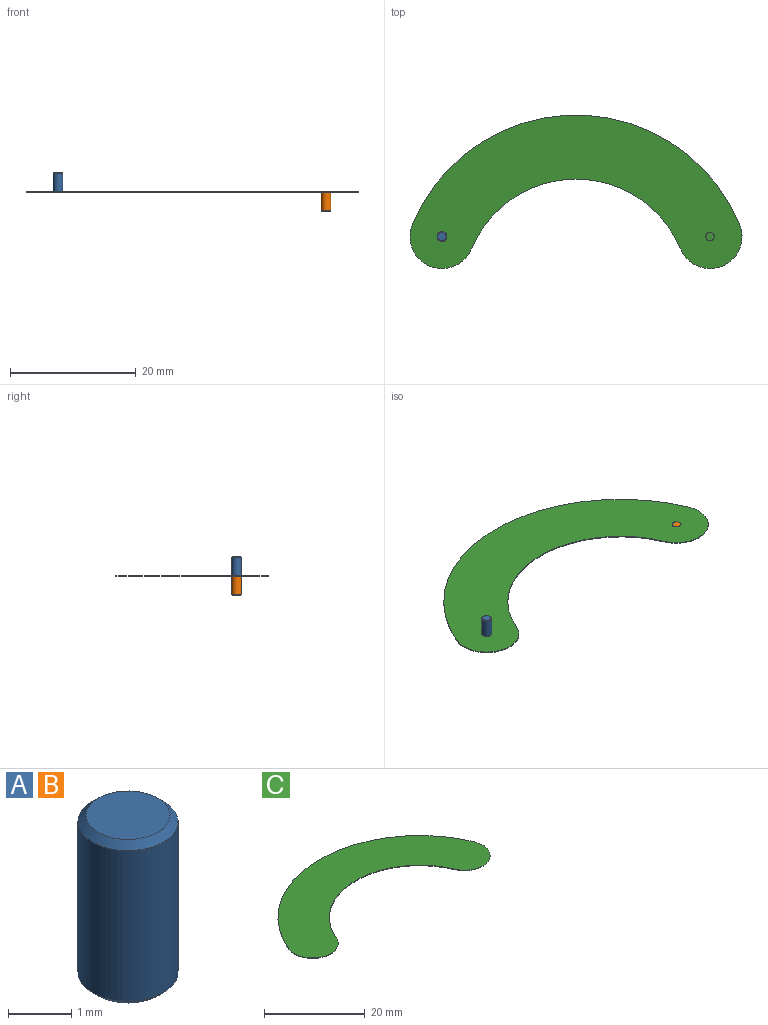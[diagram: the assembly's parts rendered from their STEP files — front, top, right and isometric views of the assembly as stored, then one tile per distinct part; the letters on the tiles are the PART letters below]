
ASSEMBLY  parts=3 mates=2
PART A: 5 faces, bbox 1.6x1.6x3.2 mm
  f0: cylinder r=0.79mm len=2.92mm, axis (0,0,-1), area 14.6mm2, adj f3,f4
  f1: plane 1.33x1.33mm, normal (0,0,1), area 1.4mm2, adj f4
  f2: plane 1.33x1.33mm, normal (0,0,-1), area 1.4mm2, adj f3
  f3: cone r=0.79mm half-angle=45deg, axis (0,0,1), area 0.8mm2, adj f0,f2
  f4: cone r=0.67mm half-angle=45deg, axis (0,0,-1), area 0.8mm2, adj f0,f1
PART B: same geometry as A
PART C: 6 faces, bbox 52.9x24.4x0.1 mm
  f0: cylinder r=18mm len=33.26mm, axis (0,0,-1), area 5.4mm2, adj f1,f3,f4,f5
  f1: cylinder r=5.1mm len=9.8mm, axis (0,0,-1), area 2mm2, adj f0,f2,f4,f5
  f2: cylinder r=28.19mm len=52.09mm, axis (0,0,-1), area 8.4mm2, adj f1,f3,f4,f5
  f3: cylinder r=5.1mm len=9.8mm, axis (0,0,-1), area 2mm2, adj f0,f2,f4,f5
  f4: plane 52.87x24.45mm, normal (0,0,1), area 636.2mm2, adj f0,f1,f2,f3
  f5: plane 52.87x24.45mm, normal (0,0,-1), area 636.2mm2, adj f0,f1,f2,f3
PLACE A rot(axis=(1,0,0),180deg) t=(-21.34,8.84,3.18)mm
PLACE B rot(axis=(1,0,0),180deg) t=(21.34,8.84,0.13)mm
PLACE C at identity fixed
MATE fastened A.f0 <-> C.f3  axis (0,0,1) through (-21.34,8.84,0.13)mm
MATE fastened B.f0 <-> C.f1  axis (0,0,-1) through (21.34,8.84,0)mm
